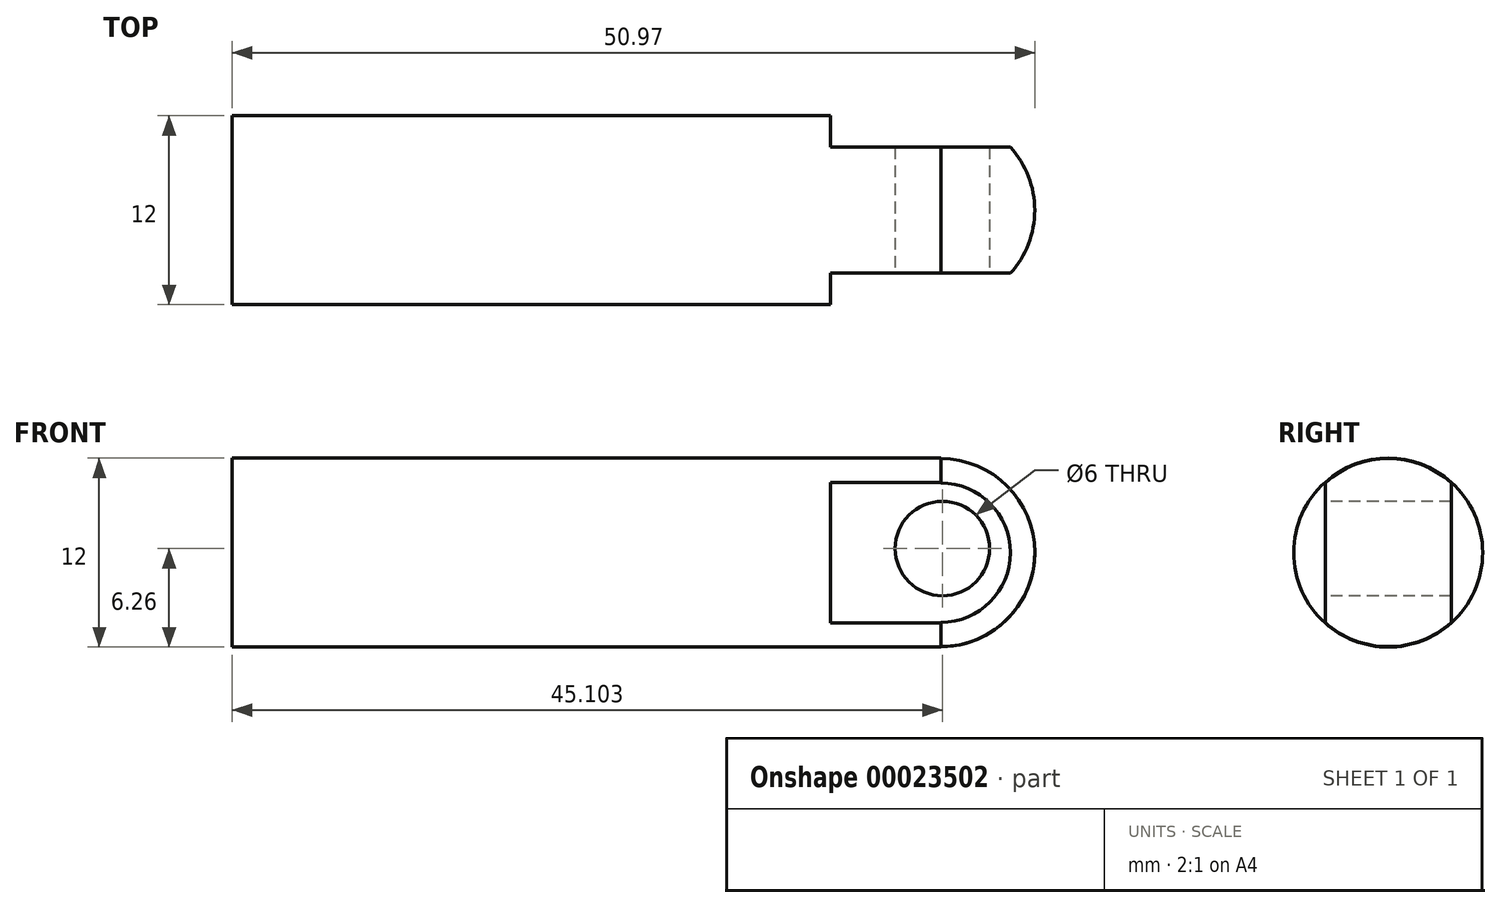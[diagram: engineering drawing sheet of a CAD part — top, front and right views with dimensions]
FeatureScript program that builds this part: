
annotation { "Feature Type Name" : "Feature", "Feature Type Description" : "" }
export const myFeature = defineFeature(function(context is Context, id is Id, definition is map)
    precondition{}
    {
        {
            var Q0;
            Q0=qCreatedBy(makeId("Front.planeOp"),FACE);
            var sketch = newSketch(context, id + "F0", { "sketchPlane" : qUnion([Q0])});
            skLineSegment(sketch, "E0.bottom", {"start": v(0, 0) * mm, "end": v(45, 0) * mm});
            skLineSegment(sketch, "E0.top", {"start": v(0, 12) * mm, "end": v(45, 12) * mm});
            skLineSegment(sketch, "E0.left", {"start": v(0, 0) * mm, "end": v(0, 12) * mm});
            skLineSegment(sketch, "E0.right", {"start": v(45, 0) * mm, "end": v(45, 0.03) * mm});
            skArc(sketch, "E1", {"start": v(45, 0.03) * mm, "mid": v(50.97, 6) * mm, "end": v(45, 11.97) * mm});
            skLineSegment(sketch, "E2.trimOffspring", {"start": v(45, 11.97) * mm, "end": v(45, 12) * mm});
            skPoint(sketch, "E3.orphan", {"position": v(0, 6) * mm});
            skLineSegment(sketch, "E4", {"start": v(50.97, 6) * mm, "end": v(0, 6) * mm});
            skSolve(sketch);
        }
        {
            var Q0;
            {var subQ6=sQuery(id+"F0.wireOp",EDGE,"E0.top");Q0=makeQuery(id+"F0.imprint","IMPRINT",FACE,{"disambiguationData":[TD([[makeQuery(id+"F0.imprint","IMPRINT",EDGE,{"derivedFrom":subQ6}),-1.0]])]});}
            var Q1;
            Q1=sQuery(id+"F0.wireOp",EDGE,"E4");
            var Q2;
            Q2=sQuery(id+"F0.wireOp",EDGE,"E4");
            revolve(context, id + "F1", {"entities" : qUnion([Q0]), "surfaceEntities" : qUnion([Q1]), "axis" : qUnion([Q2]), "revolveType" : RevolveType.FULL});
        }
        {
            var Q0;
            Q0=qCreatedBy(makeId("Front.planeOp"),FACE);
            var sketch = newSketch(context, id + "F2", { "sketchPlane" : qUnion([Q0])});
            skCircle(sketch, "E5", {"center": v(45.1, 6.26) * mm, "radius": 3 * mm});
            skSolve(sketch);
        }
        {
            var Q0;
            Q0 = qSketchRegion(id + "F2", true);
            extrude(context, id + "F3", {"entities" : qUnion([Q0]), "operationType" : NewBodyOperationType.REMOVE, "oppositeDirection" : true, "depth" : 25 * mm, "hasSecondDirection" : true, "secondDirectionOppositeDirection" : false, "secondDirectionDepth" : 25 * mm});
        }
        {
            var Q0;
            Q0=qCreatedBy(makeId("Right.planeOp"),FACE);
            cPlane(context, id + "F4", {"entities" : qUnion([Q0]), "cplaneType" : CPlaneType.OFFSET, "offset" : 38 * mm, "width" : 150 * mm, "height" : 150 * mm});
        }
        {
            var Q0;
            Q0=qCreatedBy(id+"F4.planeOp",FACE);
            var sketch = newSketch(context, id + "F5", { "sketchPlane" : qUnion([Q0])});
            skLineSegment(sketch, "E6", {"start": v(4, 25.7) * mm, "end": v(4, -10.01) * mm});
            skLineSegment(sketch, "E7", {"start": v(-4, 25.7) * mm, "end": v(-4, -3.06) * mm});
            skLineSegment(sketch, "E8", {"start": v(16.13, -10.1) * mm, "end": v(16.13, 25.5) * mm});
            skLineSegment(sketch, "E9", {"start": v(-12.8, 26.26) * mm, "end": v(-12.8, -11.12) * mm});
            skLineSegment(sketch, "E10", {"start": v(-12.8, -11.12) * mm, "end": v(-4, -3.06) * mm});
            skLineSegment(sketch, "E11", {"start": v(-12.8, 26.26) * mm, "end": v(-4, 25.7) * mm});
            skLineSegment(sketch, "E12", {"start": v(16.13, 25.5) * mm, "end": v(4, 25.7) * mm});
            skLineSegment(sketch, "E13", {"start": v(4, -10.01) * mm, "end": v(16.13, -10.1) * mm});
            skPoint(sketch, "E14.end.orphan", {"position": v(0, 26.31) * mm});
            skLineSegment(sketch, "E15", {"start": v(0, 26.31) * mm, "end": v(0, 0) * mm});
            skSolve(sketch);
        }
        {
            var Q0;
            Q0 = qSketchRegion(id + "F5", true);
            extrude(context, id + "F6", {"entities" : qUnion([Q0]), "operationType" : NewBodyOperationType.REMOVE, "depth" : 25 * mm});
        }
    });
